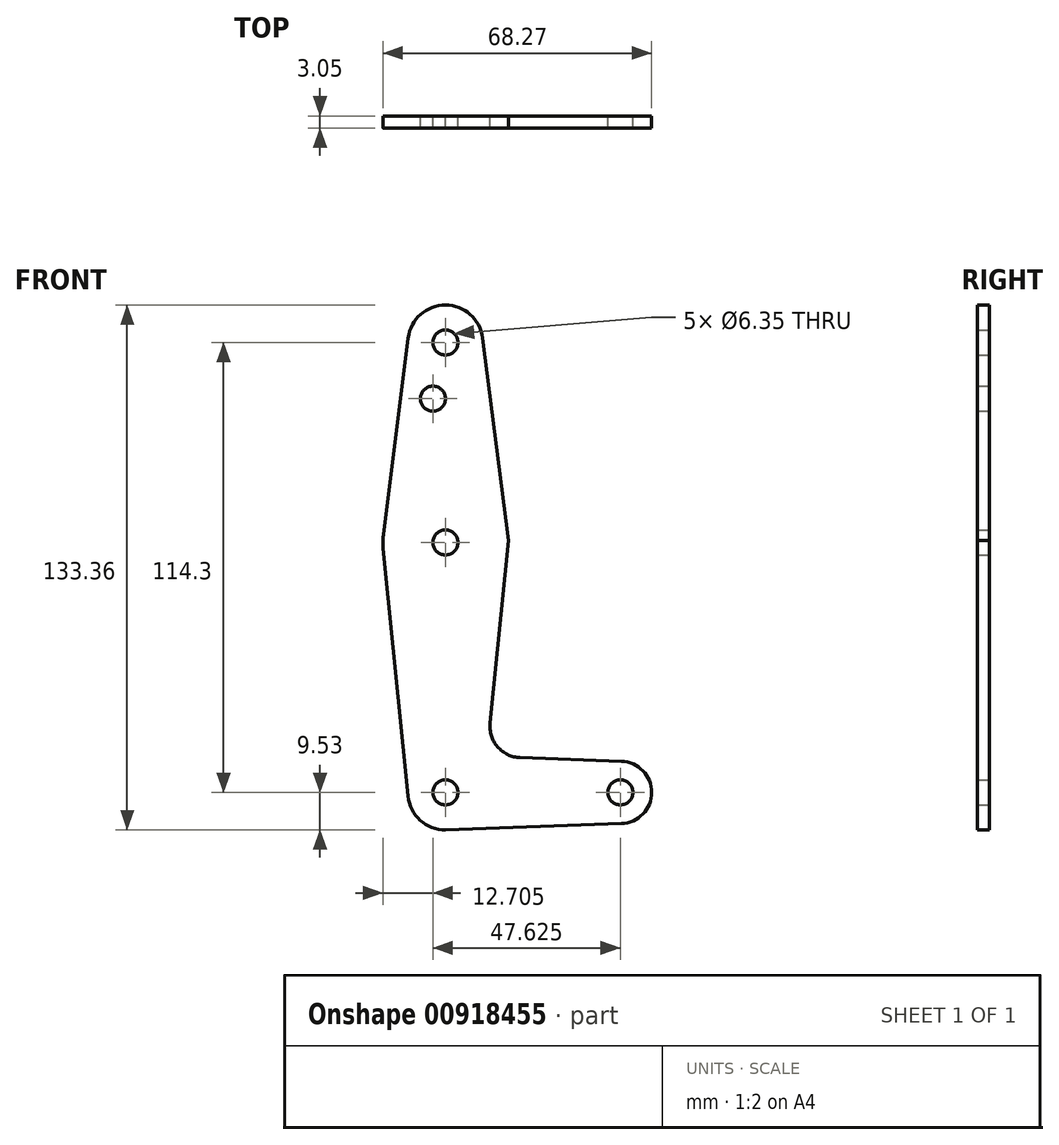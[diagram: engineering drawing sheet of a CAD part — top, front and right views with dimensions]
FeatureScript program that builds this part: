
annotation { "Feature Type Name" : "Feature", "Feature Type Description" : "" }
export const myFeature = defineFeature(function(context is Context, id is Id, definition is map)
    precondition{}
    {
        {
            var Q0;
            Q0=qCreatedBy(makeId("Front.planeOp"),FACE);
            var sketch = newSketch(context, id + "F0", { "sketchPlane" : qUnion([Q0])});
            skLineSegment(sketch, "E0", {"start": v(0, 114.3) * mm, "end": v(0, 0) * mm, "construction": true});
            skLineSegment(sketch, "E1", {"start": v(0, 0) * mm, "end": v(44.45, 0) * mm, "construction": true});
            skCircle(sketch, "E2", {"center": v(0, 114.3) * mm, "radius": 9.53 * mm});
            skCircle(sketch, "E3", {"center": v(0, 63.5) * mm, "radius": 15.88 * mm});
            skCircle(sketch, "E4", {"center": v(0, 0) * mm, "radius": 9.53 * mm});
            skCircle(sketch, "E5", {"center": v(44.45, 0) * mm, "radius": 7.94 * mm});
            skLineSegment(sketch, "E6", {"start": v(9.45, 115.5) * mm, "end": v(16, 63.98) * mm});
            skLineSegment(sketch, "E7", {"start": v(-9.45, 115.5) * mm, "end": v(-15.98, 63.7) * mm});
            skLineSegment(sketch, "E8", {"start": v(-15.98, 63.7) * mm, "end": v(-9.48, -0.95) * mm});
            skLineSegment(sketch, "E9", {"start": v(16, 63.98) * mm, "end": v(11.34, 17.59) * mm});
            skLineSegment(sketch, "E10", {"start": v(0, -9.53) * mm, "end": v(44.73, -7.93) * mm});
            skLineSegment(sketch, "E11", {"start": v(18.97, 8.85) * mm, "end": v(44.73, 7.93) * mm});
            skCircle(sketch, "E12", {"center": v(0, 114.3) * mm, "radius": 3.18 * mm});
            skCircle(sketch, "E13", {"center": v(-3.18, 100.03) * mm, "radius": 3.18 * mm});
            skCircle(sketch, "E14", {"center": v(0, 63.5) * mm, "radius": 3.18 * mm});
            skCircle(sketch, "E15", {"center": v(0, 0) * mm, "radius": 3.18 * mm});
            skCircle(sketch, "E16", {"center": v(44.45, 0) * mm, "radius": 3.18 * mm});
            skArc(sketch, "E17.filletArc", {"start": v(11.34, 17.59) * mm, "mid": v(13.26, 11.57) * mm, "end": v(18.97, 8.85) * mm});
            skSolve(sketch);
        }
        {
            var Q0;
            {var subQ12=sQuery(id+"F0.wireOp",EDGE,"E11");Q0=makeQuery(id+"F0.imprint","IMPRINT",FACE,{"disambiguationData":[TD([[makeQuery(id+"F0.imprint","IMPRINT",EDGE,{"derivedFrom":subQ12}),-1.0]])]});}
            var Q1;
            {var subQ0=sQuery(id+"F0.wireOp",EDGE,"E6");Q1=makeQuery(id+"F0.imprint","IMPRINT",FACE,{"disambiguationData":[TD([[makeQuery(id+"F0.imprint","IMPRINT",EDGE,{"derivedFrom":subQ0}),-1.0]])]});}
            var Q2;
            Q2=makeQuery(id+"F0.imprint","IMPRINT",FACE,{"disambiguationData":[TD([[makeQuery(id+"F0.imprint","IMPRINT",EDGE,{"derivedFrom":sQuery(id+"F0.wireOp",EDGE,"E14")}),-1.0]])]});
            var Q3;
            Q3=makeQuery(id+"F0.imprint","IMPRINT",FACE,{"disambiguationData":[TD([[makeQuery(id+"F0.imprint","IMPRINT",EDGE,{"derivedFrom":sQuery(id+"F0.wireOp",EDGE,"E12")}),-1.0]])]});
            var Q4;
            Q4=makeQuery(id+"F0.imprint","IMPRINT",FACE,{"disambiguationData":[TD([[makeQuery(id+"F0.imprint","IMPRINT",EDGE,{"derivedFrom":sQuery(id+"F0.wireOp",EDGE,"E15")}),-1.0]])]});
            var Q5;
            Q5=makeQuery(id+"F0.imprint","IMPRINT",FACE,{"disambiguationData":[TD([[makeQuery(id+"F0.imprint","IMPRINT",EDGE,{"derivedFrom":sQuery(id+"F0.wireOp",EDGE,"E16")}),-1.0]])]});
            extrude(context, id + "F1", {"entities" : qUnion([Q0, Q1, Q2, Q3, Q4, Q5]), "depth" : 3.05 * mm, "offsetDistance" : 25.4 * mm});
        }
    });
